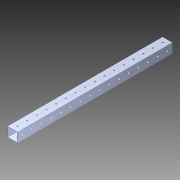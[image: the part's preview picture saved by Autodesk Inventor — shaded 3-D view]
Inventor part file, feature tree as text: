
AUTODESK INVENTOR PART (.ipt)
format: ipt  version: 2014 SP1 (Build 180222100, 222)  size: 1,162,752 bytes
history: native  units: in
note: dims shown in document units (in); Inventor stores cm internally (conversion verified against a paired STEP export)
features: pattern_circular x1, other x1, extrude x1, imported_body x1, sketch x1
ambient origin geometry x8: Origin, YZ Plane, XZ Plane, XY Plane, X Axis, Y Axis, Z Axis, Center Point
bodies: Body1 (feature_tree)
feature tree (5):
  pattern_circular  "CirPattern2"
  other  "1x1 tube1"
  extrude  "Extrusion1"  [1 undecoded]
  imported_body  "Base1"
  sketch  "Sketch1"  dims[d0=43.0in d1=0.0in]
note: 1 required parameter value undecoded (feature->parameter linkage not recoverable at this tier; creation-order binding heuristic only, values carry confidence <= 0.55)
